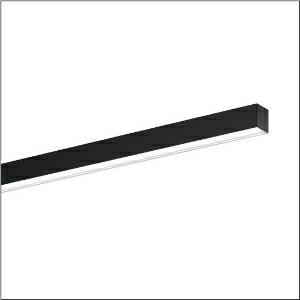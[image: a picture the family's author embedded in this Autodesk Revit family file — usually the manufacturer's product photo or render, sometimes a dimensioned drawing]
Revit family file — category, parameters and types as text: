
# Revit family: silica_r__21_51mx20da42bb_071f
name_source: partatom
category: Lighting Fixtures
units: mm (PartAtom-declared; Revit-internal decimal feet)

## family parameters
Cut with Voids When Loaded = No
Host = Face
Light Source = No
Part Type = Normal
Room Calculation Point = No
Round Connector Dimension = Use Diameter
Shared = No

## types (1)
- --- (1 x LED, 2400 lm, 15.2 W, 4000K)
    Apparent Load = 15 VA
    CIE Flux Codes = 48 79 96 100 100
    Color Rendering = 80
    Color Temperature = 4000K
    Default Elevation = 1800 mm
    Description = Silica® 21, office luminaire, primary optical cover: cover, of PMMA, opal, light emission: direct distribution, primary light characteristic: symmetric, installation type: surface-mounted, LED, rated luminous flux: 2.400lm, luminous efficacy: 158lm/W, light colour: 840, colour temperature: 4000K, control gear: DALI 2, with terminal, 3+2-pole, max. 2.5mm², mains connection: 220..240V, AC, 50/60Hz, rated input power: 15.2W, luminaire housing, of aluminium, matt jet black (RAL 9005), length: 1.204mm, width: 53mm, height: 53mm, protection rating (complete): IP20, insulation class (complete): insulation class I (protective earthing), certification: CE, permissible operating ambient temperature: 0..+35°C, standard: EN 50419, packaging unit: 1 piece
    Height = 53 mm
    Lamp = 1 x LED
    Lamp Light Flux = 2400 lm
    Lamp Power = 15.2 W
    Lamp count = 1
    Length = 1204 mm
    Luminous efficacy = 158 lm/W
    Manufacturer = Siteco
    ModVariant = No
    Model = 51MX20DA42BB
    Mounting Place = Ceiling
    Mounting Type = Surface mounted
    Number of Poles = 1
    OnlyDefault = Yes
    Power Factor = 1
    Product Name = Silica® 21
    Product group = office luminaire | ceiling mounted
    ProductGroupID = 302
    Protection Class = Protection class I
    Protection Degree = IP 20
    RLX_Detail_Level = 1
    RLX_Emergency_Light_Flux = 0 lm
    RLX_Emergency_Type = 0
    RLX_Emergency_Type_DB = No
    RlxData = <blob elided: 28753 chars, md5=904ff4f8>
    Socket = socket
    Standby Power = 0 W
    System Light Flux = 2400 lm
    System Power = 15 W
    Type Comments = factory setting: luminous flux: 100 % | dim-lin: 254 | 218 mA
    Type Image = l_1335925.jpg
    URL = http://relux.com
    VarID = @adj_007623
    Voltage = 0 V
    Weight = 0.00 kg
    Width = 53 mm

## geometry (parser evidence)
native form markers: Blend x4, Sweep x10
no freeform markers — native parametric forms only
